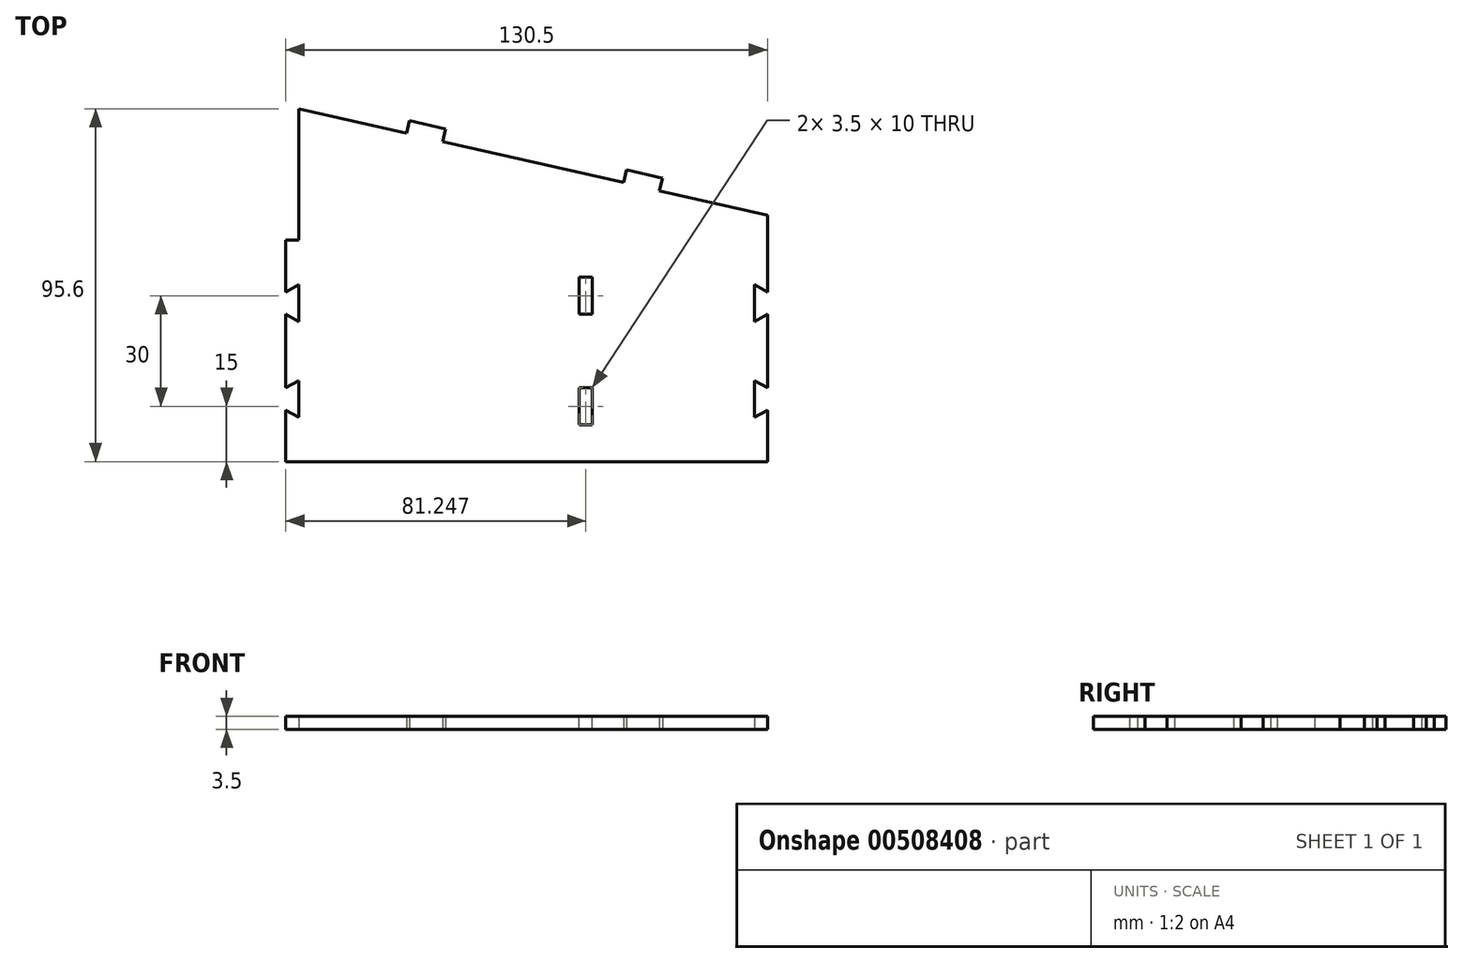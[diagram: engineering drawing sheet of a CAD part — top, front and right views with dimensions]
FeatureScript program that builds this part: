
annotation { "Feature Type Name" : "Feature", "Feature Type Description" : "" }
export const myFeature = defineFeature(function(context is Context, id is Id, definition is map)
    precondition{}
    {
        {
            var Q0;
            Q0=qCreatedBy(makeId("Top.planeOp"),FACE);
            var sketch = newSketch(context, id + "F0", { "sketchPlane" : qUnion([Q0])});
            skLineSegment(sketch, "E0", {"start": v(63.62, 0) * mm, "end": v(63.62, 6.8) * mm});
            skLineSegment(sketch, "E1", {"start": v(-63.38, 0) * mm, "end": v(-63.38, 35.6) * mm});
            skLineSegment(sketch, "E2", {"start": v(-63.38, 35.6) * mm, "end": v(-34.13, 28.97) * mm});
            skLineSegment(sketch, "E3", {"start": v(-34.13, 28.97) * mm, "end": v(-33.35, 32.38) * mm});
            skLineSegment(sketch, "E4", {"start": v(-33.35, 32.38) * mm, "end": v(-23.6, 30.17) * mm});
            skLineSegment(sketch, "E5", {"start": v(-23.6, 30.17) * mm, "end": v(-24.37, 26.75) * mm});
            skLineSegment(sketch, "E6", {"start": v(63.62, 6.8) * mm, "end": v(34.36, 13.44) * mm});
            skLineSegment(sketch, "E7", {"start": v(34.36, 13.44) * mm, "end": v(35.13, 16.85) * mm});
            skLineSegment(sketch, "E8", {"start": v(35.13, 16.85) * mm, "end": v(25.38, 19.06) * mm});
            skLineSegment(sketch, "E9", {"start": v(25.38, 19.06) * mm, "end": v(24.6, 15.65) * mm});
            skLineSegment(sketch, "E10", {"start": v(24.6, 15.65) * mm, "end": v(-24.37, 26.75) * mm});
            skLineSegment(sketch, "E11", {"start": v(63.62, -60) * mm, "end": v(-63.38, -60) * mm});
            skLineSegment(sketch, "E12", {"start": v(-66.88, 0) * mm, "end": v(-63.38, 0) * mm});
            skLineSegment(sketch, "E13", {"start": v(-66.88, -60) * mm, "end": v(-63.38, -60) * mm});
            skLineSegment(sketch, "E14", {"start": v(63.62, -60) * mm, "end": v(60.12, -60) * mm});
            skLineSegment(sketch, "E15", {"start": v(63.62, -60) * mm, "end": v(63.62, -46) * mm});
            skLineSegment(sketch, "E16", {"start": v(63.62, -40) * mm, "end": v(63.62, -20) * mm});
            skLineSegment(sketch, "E17", {"start": v(63.62, -14) * mm, "end": v(63.62, 0) * mm});
            skLineSegment(sketch, "E18", {"start": v(60.12, -48) * mm, "end": v(60.12, -38) * mm});
            skLineSegment(sketch, "E19", {"start": v(60.12, -22) * mm, "end": v(60.12, -12) * mm});
            skLineSegment(sketch, "E20", {"start": v(60.12, -12) * mm, "end": v(63.62, -14) * mm});
            skLineSegment(sketch, "E21", {"start": v(63.62, -20) * mm, "end": v(60.12, -22) * mm});
            skLineSegment(sketch, "E22", {"start": v(60.12, -38) * mm, "end": v(63.62, -40) * mm});
            skLineSegment(sketch, "E23", {"start": v(63.62, -46) * mm, "end": v(60.12, -48) * mm});
            skLineSegment(sketch, "E24", {"start": v(-63.38, -48) * mm, "end": v(-63.38, -38) * mm});
            skLineSegment(sketch, "E25", {"start": v(-63.38, -22) * mm, "end": v(-63.38, -12) * mm});
            skLineSegment(sketch, "E26", {"start": v(-66.88, -60) * mm, "end": v(-66.88, -46) * mm});
            skLineSegment(sketch, "E27", {"start": v(-66.88, -40) * mm, "end": v(-66.88, -20) * mm});
            skLineSegment(sketch, "E28", {"start": v(-66.88, -14) * mm, "end": v(-66.88, 0) * mm});
            skLineSegment(sketch, "E29", {"start": v(-63.38, -12) * mm, "end": v(-66.88, -14) * mm});
            skLineSegment(sketch, "E30", {"start": v(-66.88, -20) * mm, "end": v(-63.38, -22) * mm});
            skLineSegment(sketch, "E31", {"start": v(-63.38, -38) * mm, "end": v(-66.88, -40) * mm});
            skLineSegment(sketch, "E32", {"start": v(-66.88, -46) * mm, "end": v(-63.38, -48) * mm});
            skSolve(sketch);
        }
        {
            var Q0;
            Q0=makeQuery(id+"F0.imprint","IMPRINT",FACE,{"disambiguationData":[TD([[makeQuery(id+"F0.imprint","IMPRINT",EDGE,{"derivedFrom":sQuery(id+"F0.wireOp",EDGE,"E0")}),1.0]])]});
            extrude(context, id + "F1", {"entities" : qUnion([Q0]), "depth" : 3.5 * mm, "offsetDistance" : 25 * mm});
        }
        {
            var Q0;
            Q0=makeQuery(id+"F1.opExtrude","CAP_FACE",FACE,{"disambiguationData":[OSD([sQuery(id+"F0.wireOp",EDGE,"E0"),sQuery(id+"F0.wireOp",EDGE,"E1"),sQuery(id+"F0.wireOp",EDGE,"E2"),sQuery(id+"F0.wireOp",EDGE,"E3"),sQuery(id+"F0.wireOp",EDGE,"E4"),sQuery(id+"F0.wireOp",EDGE,"E5"),sQuery(id+"F0.wireOp",EDGE,"E6"),sQuery(id+"F0.wireOp",EDGE,"E7"),sQuery(id+"F0.wireOp",EDGE,"E8"),sQuery(id+"F0.wireOp",EDGE,"E9"),sQuery(id+"F0.wireOp",EDGE,"E10"),sQuery(id+"F0.wireOp",EDGE,"E11"),sQuery(id+"F0.wireOp",EDGE,"E12"),sQuery(id+"F0.wireOp",EDGE,"E13"),sQuery(id+"F0.wireOp",EDGE,"E14"),sQuery(id+"F0.wireOp",EDGE,"E15"),sQuery(id+"F0.wireOp",EDGE,"E16"),sQuery(id+"F0.wireOp",EDGE,"E17"),sQuery(id+"F0.wireOp",EDGE,"E18"),sQuery(id+"F0.wireOp",EDGE,"E19"),sQuery(id+"F0.wireOp",EDGE,"E20"),sQuery(id+"F0.wireOp",EDGE,"E21"),sQuery(id+"F0.wireOp",EDGE,"E22"),sQuery(id+"F0.wireOp",EDGE,"E23"),sQuery(id+"F0.wireOp",EDGE,"E24"),sQuery(id+"F0.wireOp",EDGE,"E25"),sQuery(id+"F0.wireOp",EDGE,"E26"),sQuery(id+"F0.wireOp",EDGE,"E27"),sQuery(id+"F0.wireOp",EDGE,"E28"),sQuery(id+"F0.wireOp",EDGE,"E29"),sQuery(id+"F0.wireOp",EDGE,"E30"),sQuery(id+"F0.wireOp",EDGE,"E31"),sQuery(id+"F0.wireOp",EDGE,"E32")])],"isStart":false});
            var sketch = newSketch(context, id + "F2", { "sketchPlane" : qUnion([Q0])});
            skLineSegment(sketch, "E33", {"start": v(12.62, -10) * mm, "end": v(12.62, -20) * mm});
            skLineSegment(sketch, "E34", {"start": v(12.62, -40) * mm, "end": v(12.62, -50) * mm});
            skLineSegment(sketch, "E35", {"start": v(12.62, -50) * mm, "end": v(16.12, -50) * mm});
            skLineSegment(sketch, "E36", {"start": v(16.12, -50) * mm, "end": v(16.12, -40) * mm});
            skLineSegment(sketch, "E37", {"start": v(16.12, -40) * mm, "end": v(12.62, -40) * mm});
            skLineSegment(sketch, "E38", {"start": v(12.62, -20) * mm, "end": v(16.12, -20) * mm});
            skLineSegment(sketch, "E39", {"start": v(16.12, -20) * mm, "end": v(16.12, -10) * mm});
            skLineSegment(sketch, "E40", {"start": v(16.12, -10) * mm, "end": v(12.62, -10) * mm});
            skSolve(sketch);
        }
        {
            var Q0;
            Q0=makeQuery(id+"F2.imprint","IMPRINT",FACE,{"disambiguationData":[TD([[makeQuery(id+"F2.imprint","IMPRINT",EDGE,{"derivedFrom":sQuery(id+"F2.wireOp",EDGE,"E33")}),1.0]])]});
            var Q1;
            Q1=makeQuery(id+"F2.imprint","IMPRINT",FACE,{"disambiguationData":[TD([[makeQuery(id+"F2.imprint","IMPRINT",EDGE,{"derivedFrom":sQuery(id+"F2.wireOp",EDGE,"E34")}),1.0]])]});
            extrude(context, id + "F3", {"entities" : qUnion([Q0, Q1]), "operationType" : NewBodyOperationType.REMOVE, "oppositeDirection" : true, "depth" : 3.5 * mm, "offsetDistance" : 25 * mm});
        }
    });
